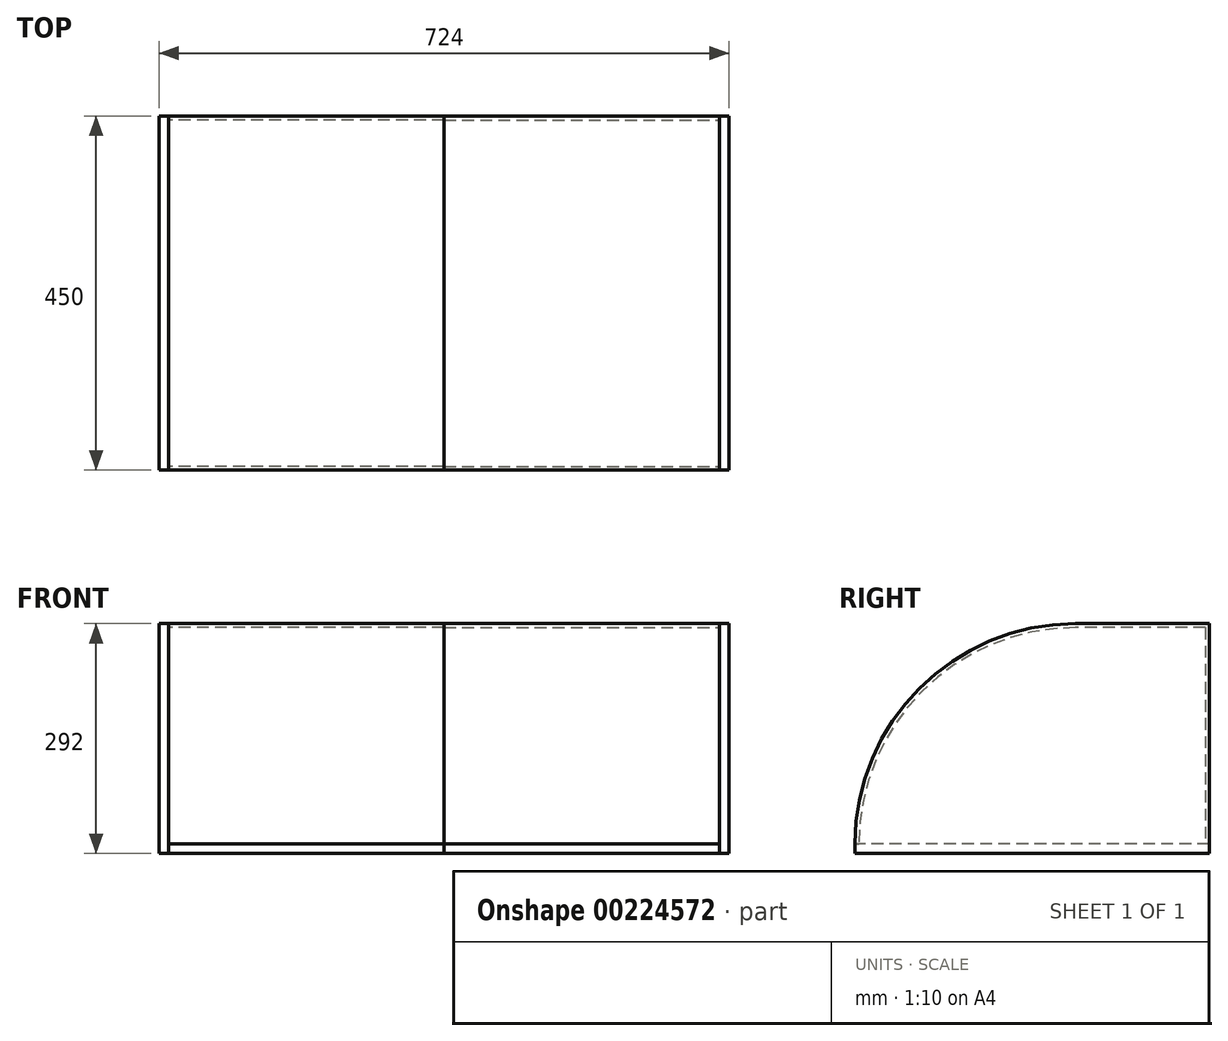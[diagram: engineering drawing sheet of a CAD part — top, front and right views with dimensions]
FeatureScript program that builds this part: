
annotation { "Feature Type Name" : "Feature", "Feature Type Description" : "" }
export const myFeature = defineFeature(function(context is Context, id is Id, definition is map)
    precondition{}
    {
        {
            assignVariable(context, id + "F0", {"name" : "Length", "anyValue" : 700});
        }
        {
            assignVariable(context, id + "F1", {"name" : "ThicknessA", "anyValue" : 12});
        }
        {
            var Q0;
            Q0=qCreatedBy(makeId("Top.planeOp"),FACE);
            var sketch = newSketch(context, id + "F2", { "sketchPlane" : qUnion([Q0])});
            skLineSegment(sketch, "E0.bottom", {"start": v(-350, 450) * mm, "end": v(0, 450) * mm});
            skLineSegment(sketch, "E0.top", {"start": v(-350, 0) * mm, "end": v(0, 0) * mm});
            skLineSegment(sketch, "E0.left", {"start": v(-350, 450) * mm, "end": v(-350, 0) * mm});
            skLineSegment(sketch, "E0.right", {"start": v(0, 450) * mm, "end": v(0, 0) * mm});
            skSolve(sketch);
        }
        {
            var Q0;
            Q0 = qSketchRegion(id + "F2", true);
            extrude(context, id + "F3", {"entities" : qUnion([Q0]), "depth" : (getVariable(context, 'ThicknessA')) * mm});
        }
        {
            var Q0;
            Q0=makeQuery(id+"F3.opExtrude","SWEPT_FACE",FACE,{"disambiguationData":[OSD([sQuery(id+"F2.wireOp",EDGE,"E0.left")])]});
            var sketch = newSketch(context, id + "F4", { "sketchPlane" : qUnion([Q0])});
            skLineSegment(sketch, "E1.0", {"start": v(-450, 0) * mm, "end": v(0, 0) * mm});
            skLineSegment(sketch, "E2", {"start": v(-450, 0) * mm, "end": v(-450, 292) * mm});
            skLineSegment(sketch, "E3", {"start": v(0, 0) * mm, "end": v(0, 12) * mm});
            skArc(sketch, "E4", {"start": v(0, 12) * mm, "mid": v(-82.01, 209.99) * mm, "end": v(-280, 292) * mm});
            skLineSegment(sketch, "E5", {"start": v(-450, 292) * mm, "end": v(-280, 292) * mm});
            skSolve(sketch);
        }
        {
            var Q0;
            Q0 = qSketchRegion(id + "F4", true);
            extrude(context, id + "F5", {"entities" : qUnion([Q0]), "depth" : (getVariable(context, 'ThicknessA')) * mm});
        }
        {
            var Q0;
            Q0=makeQuery(id+"F5.opExtrude","CAP_FACE",FACE,{"disambiguationData":[OSD([sQuery(id+"F4.wireOp",EDGE,"E1.0"),sQuery(id+"F4.wireOp",EDGE,"E2"),sQuery(id+"F4.wireOp",EDGE,"E3"),sQuery(id+"F4.wireOp",EDGE,"E4"),sQuery(id+"F4.wireOp",EDGE,"E5")])],"isStart":true});
            var sketch = newSketch(context, id + "F6", { "sketchPlane" : qUnion([Q0])});
            skLineSegment(sketch, "E6.0", {"start": v(450, 12) * mm, "end": v(0, 12) * mm, "construction": true});
            skLineSegment(sketch, "E7.0", {"start": v(445, 287) * mm, "end": v(445, 12) * mm});
            skLineSegment(sketch, "E7.1", {"start": v(445, 287) * mm, "end": v(280, 287) * mm});
            skArc(sketch, "E7.2", {"start": v(5, 12) * mm, "mid": v(85.55, 206.45) * mm, "end": v(280, 287) * mm});
            skArc(sketch, "E8.0", {"start": v(0, 12) * mm, "mid": v(82.01, 209.99) * mm, "end": v(280, 292) * mm});
            skLineSegment(sketch, "E9.0", {"start": v(450, 292) * mm, "end": v(280, 292) * mm});
            skLineSegment(sketch, "E10.0", {"start": v(450, 292) * mm, "end": v(450, 12) * mm});
            skLineSegment(sketch, "E11", {"start": v(0, 12) * mm, "end": v(5, 12) * mm});
            skLineSegment(sketch, "E12", {"start": v(450, 12) * mm, "end": v(445, 12) * mm});
            skPoint(sketch, "E13.orphan", {"position": v(450, 0) * mm});
            skSolve(sketch);
        }
        {
            var Q0;
            Q0 = qSketchRegion(id + "F6", true);
            extrude(context, id + "F7", {"entities" : qUnion([Q0]), "depth" : (getVariable(context, 'Length') / 2) * mm});
        }
        {
            var Q0;
            Q0=makeQuery(id+"F3.opExtrude","SWEPT_BODY",BODY,{"disambiguationData":[OSD([sQuery(id+"F2.wireOp",EDGE,"E0.bottom"),sQuery(id+"F2.wireOp",EDGE,"E0.top"),sQuery(id+"F2.wireOp",EDGE,"E0.left"),sQuery(id+"F2.wireOp",EDGE,"E0.right")])]});
            var Q1;
            Q1=makeQuery(id+"F5.opExtrude","SWEPT_BODY",BODY,{"disambiguationData":[OSD([sQuery(id+"F4.wireOp",EDGE,"E1.0"),sQuery(id+"F4.wireOp",EDGE,"E2"),sQuery(id+"F4.wireOp",EDGE,"E3"),sQuery(id+"F4.wireOp",EDGE,"E4"),sQuery(id+"F4.wireOp",EDGE,"E5")])]});
            var Q2;
            Q2=makeQuery(id+"F7.opExtrude","SWEPT_BODY",BODY,{"disambiguationData":[OSD([sQuery(id+"F6.wireOp",EDGE,"E7.0"),sQuery(id+"F6.wireOp",EDGE,"E7.1"),sQuery(id+"F6.wireOp",EDGE,"E7.2"),sQuery(id+"F6.wireOp",EDGE,"E8.0"),sQuery(id+"F6.wireOp",EDGE,"E9.0"),sQuery(id+"F6.wireOp",EDGE,"E10.0"),sQuery(id+"F6.wireOp",EDGE,"E11"),sQuery(id+"F6.wireOp",EDGE,"E12")])]});
            var Q3;
            Q3=makeQuery(id+"F7.opExtrude","CAP_FACE",FACE,{"disambiguationData":[OSD([sQuery(id+"F6.wireOp",EDGE,"E7.0"),sQuery(id+"F6.wireOp",EDGE,"E7.1"),sQuery(id+"F6.wireOp",EDGE,"E7.2"),sQuery(id+"F6.wireOp",EDGE,"E8.0"),sQuery(id+"F6.wireOp",EDGE,"E9.0"),sQuery(id+"F6.wireOp",EDGE,"E10.0"),sQuery(id+"F6.wireOp",EDGE,"E11"),sQuery(id+"F6.wireOp",EDGE,"E12")])],"isStart":false});
            mirror(context, id + "F8", {"entities" : qUnion([Q0, Q1, Q2]), "mirrorPlane" : qUnion([Q3])});
        }
    });
